# Revit family: 794450
name_source: partatom
category: Plumbing Fixtures
revit_build: Autodesk Revit 2015 (Build: 20140606_1530(x64)
units: mm (PartAtom-declared; Revit-internal decimal feet)

## types (1)
- Type 1
    Category = Shower mixer
    DLB090004 = Brass, Chrome plated
    Description = French manufacturer Delabie is a leader in the European sanitary ware market for non-domestic places. Water controls, solutions for disabled people, sanitary ware, for schools, leisure centres, offices, hospitals, airports…
    Diameter = 60 mm  [stored 0.19685 ft]
    Features = Time flow shower kit for wall-mounted exposed installation: Shower column link Ø 16mm with reinforced collar (fixing plate and screws included). TEMPOMIX 3 single control mixer ¾". Temperature control and operation via the push-button. Maximum temperature limiter (can be adjusted by the installer). Soft-touch operation. Time flow pre-set at ~30 sec., can be adjusted 20 - 30 sec. Flow rate 6 lpm at 3 bar. Chrome-plated, tamperproof shower head with scale-resistant nozzle and automatic flow rate regulation. Chrome-plated solid brass. Integrated filters and non-return valves. Chrome-plated metal push-button. Angled connectors, M½".
    Finish = Chrome-plated
    FlowRate = 6 lpm at 3 bar
    IntegralAccessoryOptions = Thermostatic mixing valve
    Manufacturer = DELABIE
    ManufacturerName = DELABIE
    Material = Solid brass
    Model = TEMPOMIX 3
    Model number = 794450
    Name = 794450
    NominalHeight = 100 cm
    NominalLength = 13 cm
    NominalWidth = 15 cm
    Operation = Single control time flow mixer
    Polantis code = DLB090004
    ProductInformation = http://www.delabie.com
    SerialNumber = 3456330167284
    URL = http://www.delabie.com
    WarrantyDescription = Any manufacturing defect
    WarrantyDurationUnit = 10 years
    WaterSupplyTemperatureMaximum = 55°C-85° (∆50°C : CW/HW)

note: [stored X ft] marks values corroborated as IEEE doubles in the binary element streams (Revit-internal decimal feet)

## geometry (parser evidence)
native form markers: Sweep x3
no freeform markers — native parametric forms only
